# Revit family: PGV-201G
name_source: partatom
category: Pipe Accessories
revit_build: Autodesk Revit 2017 (Build: 20160225_1515(x64)
units: mm (PartAtom-declared; Revit-internal decimal feet)

## family parameters
Always vertical = Yes
Cut with Voids When Loaded = Yes
OmniClass Number = 23.27.31.27
OmniClass Title = Globe Valves
Part Type = Valve - Normal
Round Connector Dimension = Use Diameter
Shared = Yes
Work Plane-Based = No

## types (12) — shared parameters
Assembly Code = G2050700
Body Material = Hunter® ABS Plastic
Current = 0 A
Flow Max = 775.0 L/min
Flow Min = 75.0 L/min
Frequency = 50 Hz
Height = 200 mm  [stored 0.656168 ft]
Inlet Diameter = 2" (50mm)
Inner Diameter = 50 mm  [stored 0.164042 ft]
Keynote = 328423.01 , 333100.03
Length = 170 mm  [stored 0.557743 ft]
Loss Method = K Coefficient
Manufacturer = Hunter® Industries
Max_Pressure = 1000.0 kPa
Min_Pressure = 150.0 kPa
Outer Diameter = 63 mm  [stored 0.206693 ft]
Pipe Diameter = 63 mm  [stored 0.206693 ft]
Power = 9 VA
Power Factor = 1
Show Valve Box = Yes
Solenoid VAC = 24 V
Thread = BSP Thread
Type Comments = PGV Valve
Type Image = <None>
URL = https://www.hunterindustries.com
Valve Box = Valve Box
Width = 130 mm  [stored 0.426509 ft]
zero-valued in all types: K Coefficient

## per-type parameters (varying)
| type | Accu Sync® | Accu-Sync URL | AccuSync | Description | Flow | Flow_Value | Flow_Value 2 | Model | Pressure Loss | Solenoid Type | Tag Name | Valid Flow |
| PGV-201-B |  | ------- | without AccuSync | Heavy duty, Reliable valve for long lasting performance PGV-201-B | 150.0 L/min | 150 | 150.0 L/min | PGV-201-B | 12.0 kPa | 370mA inrush | PGV-201-B | 150.0 L/min |
| PGV-201-B-AS-30 Red-2.1bar | Accu Sync® AS-30 Red Fixed Pressure Regulator at 2.1 bar | https://www.hunterindustries.com | AccuSync fixed | Heavy duty, Reliable valve for long lasting performance PGV-201-B with Accu Sync® AS-30 Red Fixed Pressure Regulator | 150.0 L/min | 150 | 150.0 L/min | PGV-201-B-AS-30 | 12.0 kPa | 370mA inrush | PGV-201-B-AS-30 | 150.0 L/min |
| PGV-201-B-AS-40 Grey-2.8bar | Accu Sync® AS-40 Grey Fixed Pressure Regulator at 2.8 bar | https://www.hunterindustries.com | AccuSync fixed | Heavy duty, Reliable valve for long lasting performance PGV-201-B with Accu Sync® AS-40 Grey Fixed Pressure Regulator | 150.0 L/min | 150 | 150.0 L/min | PGV-201-B-AS-40 | 12.0 kPa | 370mA inrush | PGV-201-B-AS-40 | 150.0 L/min |
| PGV-201-B-AS-50 Blue-3.5bar | Accu Sync® AS-50 Blue Fixed Pressure Regulator at 3.5 bar | https://www.hunterindustries.com | AccuSync fixed | Heavy duty, Reliable valve for long lasting performance PGV-201-B with Accu Sync® AS-50 Blue Fixed Pressure Regulator | 150.0 L/min | 150 | 150.0 L/min | PGV-201-B-AS-50 | 12.0 kPa | 370mA inrush | PGV-201-B-AS-50 | 150.0 L/min |
| PGV-201-B-AS-70 Green-4.8bar | Accu Sync® AS-70 Green Fixed Pressure Regulator at 4.8 bar | https://www.hunterindustries.com | AccuSync fixed | Heavy duty, Reliable valve for long lasting performance PGV-201-B with Accu Sync® AS-70 Green Fixed Pressure Regulator | 150.0 L/min | 150 | 150.0 L/min | PGV-201-B-AS-70 | 12.0 kPa | 370mA inrush | PGV-201-B-AS-70 | 150.0 L/min |
| PGV-201-B-DC |  | ------- | without AccuSync | Heavy duty, Reliable valve for long lasting performance PGV-201-B-DC with DC-latching solenoid | 150.0 L/min | 150 | 150.0 L/min | PGV-201-B-DC | 12.0 kPa | DC-latching Solenoid | PGV-201-B-DC | 150.0 L/min |
| PGV-201-B-DC-AS-30 Red-2.1bar | Accu Sync® AS-30 Red Fixed Pressure Regulator at 2.1 bar | https://www.hunterindustries.com | AccuSync fixed | Heavy duty, Reliable valve for long lasting performance PGV-201-B with DC-latching Solenoid and Accu Sync® AS-30 Red Fixed Pressure Regulator | 150.0 L/min | 150 | 150.0 L/min | PGV-201-B-DC-AS-30 | 12.0 kPa | DC-latching Solenoid | PGV-201-B-DC-AS-30 | 150.0 L/min |
| PGV-201-B-DC-AS-40 Grey-2.8bar | Accu Sync® AS-40 Grey Fixed Pressure Regulator at 2.8 bar | https://www.hunterindustries.com | AccuSync fixed | Heavy duty, Reliable valve for long lasting performance PGV-201-B with DC-latching Solenoid and Accu Sync® AS-40 Grey Fixed Pressure Regulator | 150.0 L/min | 150 | 150.0 L/min | PGV-201-B-DC-AS-40 | 12.0 kPa | DC-latching Solenoid | PGV-201-B-DC-AS-40 | 150.0 L/min |
| PGV-201-B-DC-AS-50 Blue-3.5bar | Accu Sync® AS-50 Blue Fixed Pressure Regulator at 3.5 bar | https://www.hunterindustries.com | AccuSync fixed | Heavy duty, Reliable valve for long lasting performance PGV-201-B with DC-latching Solenoid and Accu Sync® AS-50 Blue Fixed Pressure Regulator | 150.0 L/min | 150 | 150.0 L/min | PGV-201-B-DC-AS-50 | 12.0 kPa | DC-latching Solenoid | PGV-201-B-DC-AS-50 | 150.0 L/min |
| PGV-201-B-DC-AS-70 Green-4.8bar | Accu Sync® AS-70 Green Fixed Pressure Regulator at 4.8 bar | https://www.hunterindustries.com | AccuSync fixed | Heavy duty, Reliable valve for long lasting performance PGV-201-B with DC-latching Solenoid and Accu Sync® AS-70 Green Fixed Pressure Regulator | 150.0 L/min | 150 | 150.0 L/min | PGV-201-B-DC-AS-70 | 12.0 kPa | DC-latching Solenoid | PGV-201-B-DC-AS-70 | 150.0 L/min |
| PGV-201-B-AS-ADJ Black-Adjustable Pressure | Accu Sync® AS-ADJ Black Adjustable Pressure Regulator | https://www.hunterindustries.com | AccuSync Adjustable | Heavy duty, Reliable valve for long lasting performance PGV-201-B with Accu Sync® AS-ADJ Black Adjustable Pressure Regulator | 190.0 L/min | 190 | 190.0 L/min | PGV-201-B-AS-ADJ | 13.6 kPa | 370mA inrush | PGV-201-B-AS-ADJ | 190.0 L/min |
| PGV-201-B-DC-AS-ADJ Black-Adjustable Pressure | Accu Sync® AS-ADJ Black Adjustable Pressure Regulator | https://www.hunterindustries.com | AccuSync Adjustable | Heavy duty, Reliable valve for long lasting performance PGV-201-B with DC-latching Solenoid and Accu Sync® AS-ADJ Black Adjustable Pressure Regulator | 700.0 L/min | 700 | 700.0 L/min | PGV-201-B-DC-AS-ADJ | 65.0 kPa | DC-latching Solenoid | PGV-201-B-DC-AS-ADJ | 700.0 L/min |

note: [stored X ft] marks values corroborated as IEEE doubles in the binary element streams (Revit-internal decimal feet)

## geometry (parser evidence)
native form markers: Sweep x32
no freeform markers — native parametric forms only
